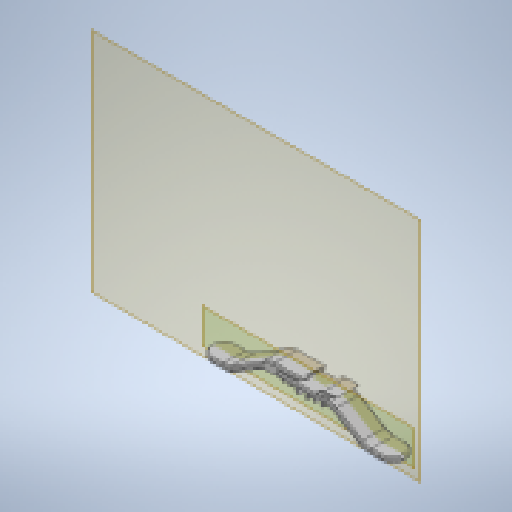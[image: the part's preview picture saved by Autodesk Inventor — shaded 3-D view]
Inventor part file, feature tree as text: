
AUTODESK INVENTOR PART (.ipt)
format: ipt  version: 2023 (Build 270158030, 158C)  size: 588,288 bytes
history: native  units: mm
features: fillet x7, extrude x5, chamfer x5, other x4, sketch x4, projected_geometry x3, plane x2, reference x2
ambient origin geometry x8: Origin, YZ Plane, XZ Plane, XY Plane, X Axis, Y Axis, Z Axis, Center Point
bodies: Body1 (feature_tree)
feature tree (32):
  other  "cable-hanger"
  extrude  "Extrusion1"  Depth=1.0mm TaperAngle=0.0deg
  fillet  "Fillet1"  Radius=7.5mm
  fillet  "Fillet2"  Radius=10.0mm
  chamfer  "Chamfer1"  Distance=1.0mm Angle=45.0deg
  plane  "Work Plane1"
  extrude  "Extrusion2"  Depth=5.0mm
  fillet  "Fillet3"  Radius=6.0mm
  fillet  "Fillet4"  Radius=4.0mm
  chamfer  "Chamfer2"  Distance=40.0mm
  plane  "Work Plane2"
  extrude  "Extrusion3"  Depth=1.0mm
  chamfer  "Chamfer3"  Distance=9.5mm
  chamfer  "Chamfer4"  Distance=1.2mm
  extrude  "Extrusion4"  Depth=1.0mm
  fillet  "Fillet5"  Radius=1.2mm
  fillet  "Fillet6"  Radius=2.5mm
  chamfer  "Chamfer5"  Distance=1.25mm
  extrude  "Extrusion5"  Depth=1.0mm
  fillet  "Fillet7"  Radius=1.5mm
  sketch  "Sketch1"  dims[d0=3.0mm d1=3.0mm d2=3.0mm d3=17.0mm d4=-20.0mm d5=-12.0mm d6=20.0mm d7=114.0mm d8=20.0mm d9=-20.0mm d10=17.0mm d11=2.0mm d12=1.5mm d13=10.0mm d14=15.0mm d15=0.0mm d16=7.5mm d17=10.0mm d18=1.0mm d19=2.0mm d20=45.0deg]
  sketch  "Sketch2"  dims[d21=10.0mm d22=10.0mm d23=7.210321mm d24=7.25mm d25=3.3mm d26=4.0mm d27=5.0mm d28=1.2mm d29=1.2mm d30=1.2mm d31=2.5mm d32=1.25mm d33=1.65mm d34=0.825mm d35=2.0mm d36=1.0mm]
  projected_geometry  "Projected Loop1"
  projected_geometry  "Projected Loop2"
  projected_geometry  "Projected Loop3"
  reference  "Reference1"
  reference  "Reference2"
  sketch  "Sketch4"  dims[d37=10.0mm d38=10.0mm d39=7.210321mm d40=7.25mm d41=3.3mm d42=4.0mm d43=5.0mm d44=1.2mm d45=1.2mm d46=1.2mm d47=2.5mm d48=1.25mm d49=1.65mm d50=0.825mm d51=2.0mm d52=1.0mm d53=5.0mm d54=6.0mm d55=4.0mm]
  sketch  "Sketch5"  dims[d56=40.0mm d57=40.0mm d58=9.5mm d59=9.5mm d60=1.2mm d61=1.2mm d62=1.2mm d63=2.5mm d64=1.25mm d65=3.0mm d66=1.5mm d67=2.0mm d68=1.0mm d69=8.0mm d70=0.0mm d71=1.0mm d72=1.0mm d73=1.0mm d74=2.0mm d75=45.0deg d76=2.5mm d78=8.0mm d79=0.0mm d80=1.6mm d81=2.0mm d82=45.0deg d83=0.5mm d84=2.0mm d85=45.0deg d86=15.0mm d87=13.8mm d88=1.0mm d89=22.0mm d90=4.0mm d91=12.0mm d92=14.0mm d93=0.0mm d94=10.0mm d95=5.0mm d96=0.5mm d97=2.0mm d98=45.0deg d99=2.0mm d100=4.25mm d101=8.0mm d102=0.0mm d103=1.0mm]
  other  "<userpath>\Documents\0004-inventor\3D-CAD-main\cable-hanger\cable-hanger-hook.iam"
  other  "cable-hanger-hook.iam"
  other  "backplate-0:1"
